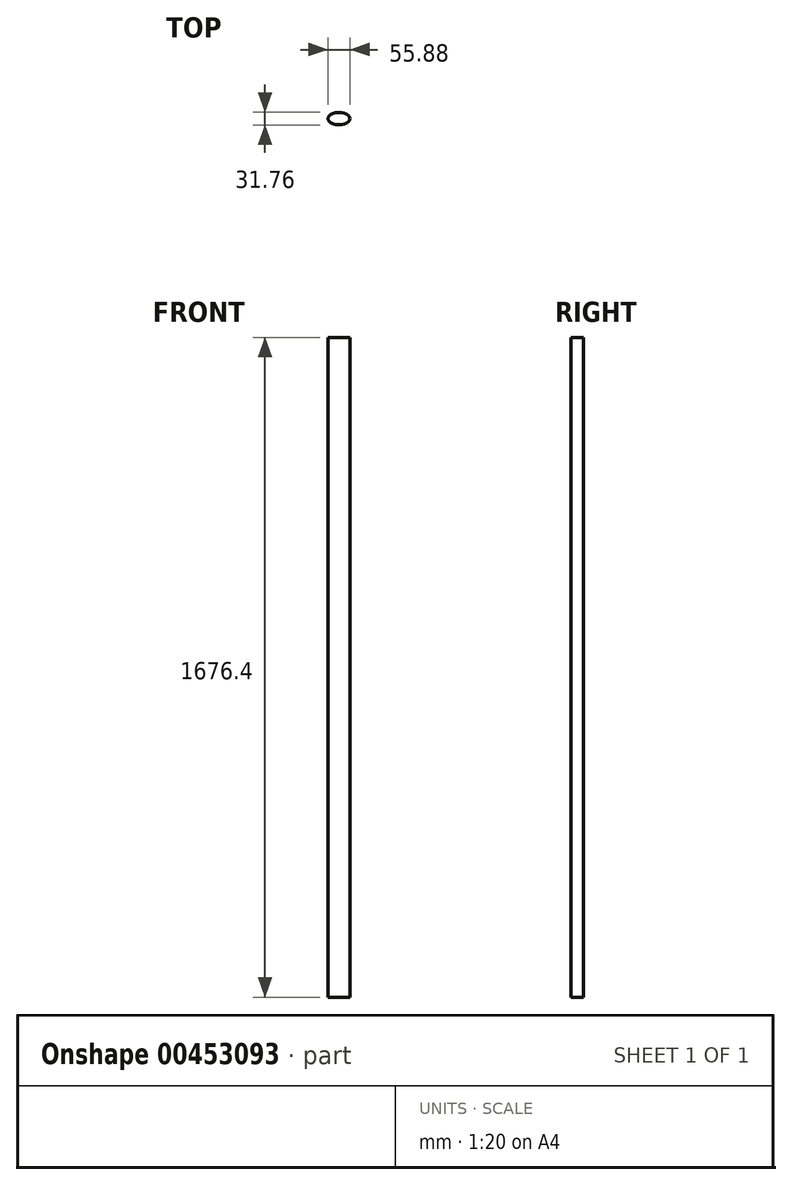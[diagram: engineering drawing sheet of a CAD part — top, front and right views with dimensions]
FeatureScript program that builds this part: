
annotation { "Feature Type Name" : "Feature", "Feature Type Description" : "" }
export const myFeature = defineFeature(function(context is Context, id is Id, definition is map)
    precondition{}
    {
        {
            var Q0;
            Q0=qCreatedBy(makeId("Top.planeOp"),FACE);
            var sketch = newSketch(context, id + "F0", { "sketchPlane" : qUnion([Q0])});
            skEllipse(sketch, "E0", {"center": v(0, 0) * mm, "majorRadius": 27.94 * mm, "minorRadius": 15.87 * mm, "majorAxis": v(1, 0)});
            skSolve(sketch);
        }
        {
            var Q0;
            Q0 = qSketchRegion(id + "F0", true);
            extrude(context, id + "F1", {"entities" : qUnion([Q0]), "depth" : 1676.4 * mm});
        }
    });
